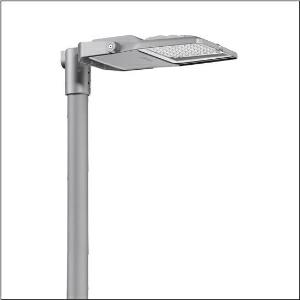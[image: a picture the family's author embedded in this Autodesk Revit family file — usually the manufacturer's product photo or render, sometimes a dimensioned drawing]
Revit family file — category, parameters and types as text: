
# Revit family: floodlight_fl_21_mini___pl64_5xa7776d2e3a_9c1a
name_source: partatom
category: Lighting Fixtures
units: mm (PartAtom-declared; Revit-internal decimal feet)

## family parameters
Cut with Voids When Loaded = No
Host = Face
Light Source = No
Part Type = Normal
Room Calculation Point = No
Round Connector Dimension = Use Diameter
Shared = No

## types (1)
- --- (1 x LED, 17220 lm, 142.9 W, 3000K)
    Apparent Load = 143 VA
    CIE Flux Codes = 28 80 98 100 100
    Color Rendering = 70
    Color Temperature = 3000K
    Default Elevation = 1800 mm
    Description = Floodlight FL 21 mini, floodlight, primary light control with lens, of PMMA, primary optical cover: protective disc, of toughened safety glass, transparent, light distribution: PL64, light emission: direct distribution, installation type: surface-mounted, LED, High Power LED, rated luminous flux: 17.220lm, luminous efficacy: 121lm/W, light colour: 730, colour temperature: 3000K, control: flexible luminous flux parameterisation, time-dependent luminous flux control, constant luminous flux control, overheat protection, presetting dimming logarithmic, with terminal, 6-pole, mains connection: 220..240V, AC, 50/60Hz, start of lifetime: 143W, end of service life: 151W, reduction: 63W, luminaire housing, of diecast aluminium, powder-coated, Siteco® metallic grey (DB 702S), corrosivity category C5 mid according to DIN EN ISO 12944, sealing non-destructively replaceable, please order mast flange separately, mast bracket, of steel, galvanised, powder-coated, Siteco® metallic grey (DB 702S), Smart Interface below and above, protection rating (complete): IP66, insulation class (complete): insulation class II (safety insulation), certification: CE, ENEC, VDE, protection symbol: D, impact resistance: IK08, permissible operating ambient temperature: -40..+40°C, permissible operating ambient temperature for outdoor applications: -40..+50°C, standard: DIN EN 12944, LABS conformity tested according to VDMA 24364:2018-05, packaging unit: 1 piece

Light Distribution: PL64
    Height = 70 mm
    Lamp = 1 x LED
    Lamp Light Flux = 17220 lm
    Lamp Power = 142.9 W
    Lamp count = 1
    Length = 485 mm
    Luminous efficacy = 121 lm/W
    Manufacturer = Siteco
    ModVariant = No
    Model = 5XA7776D2E3A
    Number of Poles = 1
    OnlyDefault = Yes
    Power Factor = 1
    Product Name = Floodlight FL 21 mini | PL64
    Product group = floodlight | pylon annexe
    ProductGroupID = 6200
    Protection Class = Protection class II
    Protection Degree = IP 66
    RLX_Detail_Level = 1
    RLX_Emergency_Light_Flux = 0 lm
    RLX_Emergency_Type = 0
    RLX_Emergency_Type_DB = No
    RlxData = <blob elided: 101221 chars, md5=5ac72988>
    Socket = socket
    Standby Power = 0 W
    System Light Flux = 17220 lm
    System Power = 143 W
    Type Comments = factory setting: luminous flux: 100 % | dim-lin: 254 | 730 mA
    Type Image = l_1007125.jpg
    URL = http://relux.com
    VarID = @adj_115355
    Voltage = 0 V
    Weight = 0.00 kg
    Width = 337 mm

## geometry (parser evidence)
native form markers: Blend x4, Sweep x12
no freeform markers — native parametric forms only
